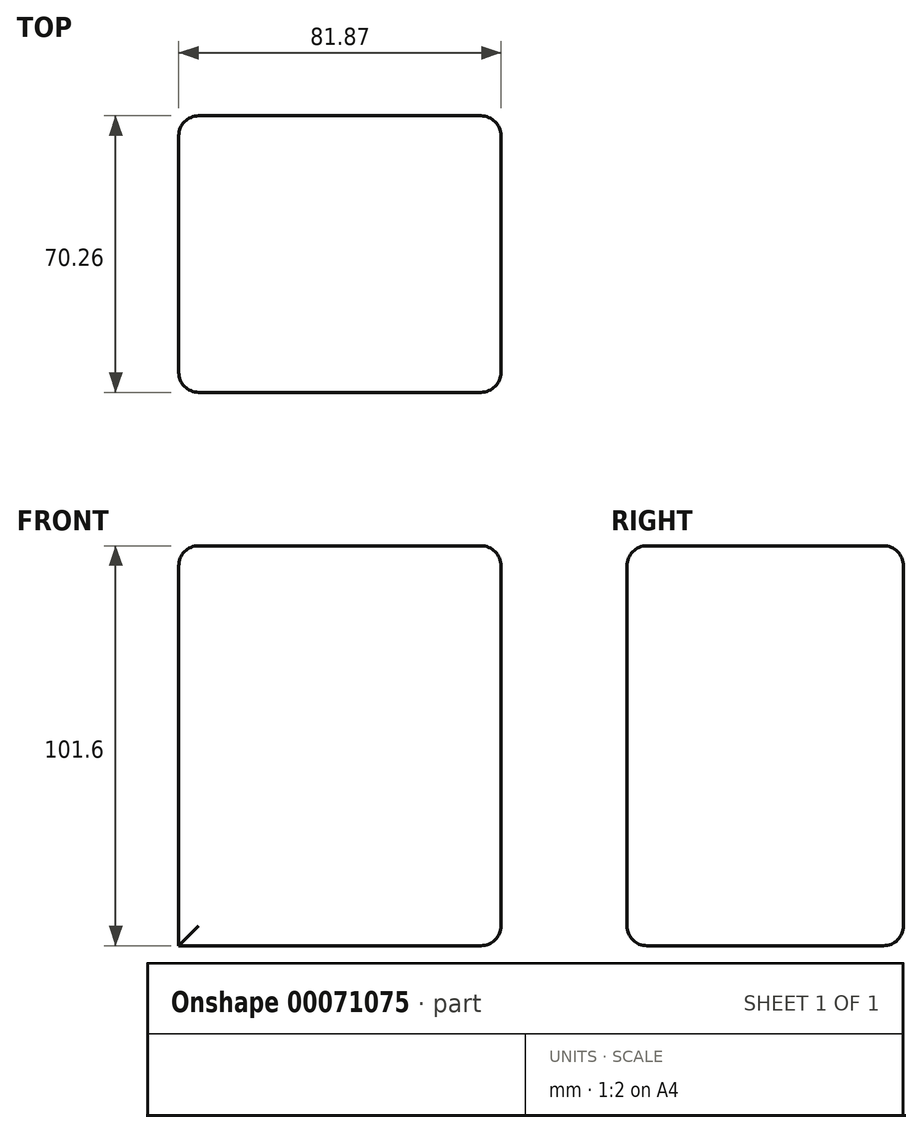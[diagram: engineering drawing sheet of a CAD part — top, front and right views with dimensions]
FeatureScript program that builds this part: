
annotation { "Feature Type Name" : "Feature", "Feature Type Description" : "" }
export const myFeature = defineFeature(function(context is Context, id is Id, definition is map)
    precondition{}
    {
        {
            var Q0;
            Q0=qCreatedBy(makeId("Top.planeOp"),FACE);
            var sketch = newSketch(context, id + "F0", { "sketchPlane" : qUnion([Q0])});
            skLineSegment(sketch, "E0.bottom", {"start": v(-51.3, 42.52) * mm, "end": v(30.56, 42.52) * mm});
            skLineSegment(sketch, "E0.top", {"start": v(-51.3, -27.74) * mm, "end": v(30.56, -27.74) * mm});
            skLineSegment(sketch, "E0.left", {"start": v(-51.3, 42.52) * mm, "end": v(-51.3, -27.74) * mm});
            skLineSegment(sketch, "E0.right", {"start": v(30.56, 42.52) * mm, "end": v(30.56, -27.74) * mm});
            skSolve(sketch);
        }
        {
            var Q0;
            Q0=makeQuery(id+"F0.imprint","IMPRINT",FACE,{"disambiguationData":[TD([[makeQuery(id+"F0.imprint","IMPRINT",EDGE,{"derivedFrom":sQuery(id+"F0.wireOp",EDGE,"E0.bottom")}),-1.0]])]});
            extrude(context, id + "F1", {"entities" : qUnion([Q0]), "depth" : 101.6 * mm});
        }
        {
            var Q0;
            Q0=makeQuery(id+"F1.opExtrude","CAP_EDGE",EDGE,{"disambiguationData":[OSD([sQuery(id+"F0.wireOp",EDGE,"E0.top")])],"isStart":false});
            var Q1;
            Q1=makeQuery(id+"F1.opExtrude","CAP_EDGE",EDGE,{"disambiguationData":[OSD([sQuery(id+"F0.wireOp",EDGE,"E0.right")])],"isStart":false});
            var Q2;
            Q2=makeQuery(id+"F1.opExtrude","SWEPT_EDGE",EDGE,{"disambiguationData":[OSD([sQuery(id+"F0.wireOp",EDGE,"E0.top"),sQuery(id+"F0.wireOp",EDGE,"E0.right")])]});
            var Q3;
            Q3=makeQuery(id+"F1.opExtrude","SWEPT_EDGE",EDGE,{"disambiguationData":[OSD([sQuery(id+"F0.wireOp",EDGE,"E0.top"),sQuery(id+"F0.wireOp",EDGE,"E0.left")])]});
            var Q4;
            Q4=makeQuery(id+"F1.opExtrude","CAP_EDGE",EDGE,{"disambiguationData":[OSD([sQuery(id+"F0.wireOp",EDGE,"E0.left")])],"isStart":false});
            var Q5;
            Q5=makeQuery(id+"F1.opExtrude","CAP_EDGE",EDGE,{"disambiguationData":[OSD([sQuery(id+"F0.wireOp",EDGE,"E0.bottom")])],"isStart":false});
            var Q6;
            Q6=makeQuery(id+"F1.opExtrude","SWEPT_EDGE",EDGE,{"disambiguationData":[OSD([sQuery(id+"F0.wireOp",EDGE,"E0.bottom"),sQuery(id+"F0.wireOp",EDGE,"E0.right")])]});
            var Q7;
            Q7=makeQuery(id+"F1.opExtrude","CAP_EDGE",EDGE,{"disambiguationData":[OSD([sQuery(id+"F0.wireOp",EDGE,"E0.right")])],"isStart":true});
            var Q8;
            Q8=makeQuery(id+"F1.opExtrude","CAP_EDGE",EDGE,{"disambiguationData":[OSD([sQuery(id+"F0.wireOp",EDGE,"E0.top")])],"isStart":true});
            var Q9;
            Q9=makeQuery(id+"F1.opExtrude","CAP_EDGE",EDGE,{"disambiguationData":[OSD([sQuery(id+"F0.wireOp",EDGE,"E0.bottom")])],"isStart":true});
            var Q10;
            Q10=makeQuery(id+"F1.opExtrude","SWEPT_EDGE",EDGE,{"disambiguationData":[OSD([sQuery(id+"F0.wireOp",EDGE,"E0.bottom"),sQuery(id+"F0.wireOp",EDGE,"E0.left")])]});
            fillet(context, id + "F2", {"entities" : qUnion([Q0, Q1, Q2, Q3, Q4, Q5, Q6, Q7, Q8, Q9, Q10]), "radius" : 5.08 * mm, "tangentPropagation" : true, "allowEdgeOverflow" : false});
        }
    });
